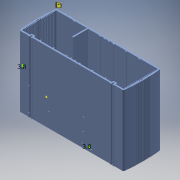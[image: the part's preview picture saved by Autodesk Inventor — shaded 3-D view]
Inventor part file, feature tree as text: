
AUTODESK INVENTOR PART (.ipt)
format: ipt  version: 2018 (Build 220112000, 112)  size: 1,293,312 bytes
history: native  units: mm
features: sketch x13, reference x7, extrude x6, other x4, projected_geometry x2, imported_body x1
ambient origin geometry x8: Origin, YZ Plane, XZ Plane, XY Plane, X Axis, Y Axis, Z Axis, Center Point
bodies: Body1 (feature_tree)
feature tree (33):
  other  "041800222_Profil_X_Dream_t220.1"
  imported_body  "Basis1"
  extrude  "Extrusion1"  Depth=4.2mm
  extrude  "Extrusion2"  Depth=93.5mm
  extrude  "Extrusion3"  Depth=8.0mm
  sketch  "Sketch5"  dims[d8=8.0mm d9=4.0mm d10=0.0mm]
  sketch  "Sketch6"  dims[d11=15.08mm d13=3.0mm]
  sketch  "Sketch7"  dims[d14=8.0mm d15=93.297949mm]
  sketch  "Sketch8"  dims[d16=3.0mm]
  sketch  "Sketch9"  dims[d17=8.0mm]
  extrude  "Extrusion6"  Depth=4.0mm TaperAngle=0.0deg
  sketch  "Sketch11"  dims[d20=3.8mm]
  sketch  "Sketch12"  dims[d23=3.8mm]
  extrude  "Extrusion7"  Depth=3.0mm
  extrude  "Extrusion9"  Depth=93.297949mm
  sketch  "Sketch2"  dims[d0=32.0mm d1=0.0mm d2=4.2mm]
  sketch  "Sketch3"  dims[d3=15.08mm d4=93.5mm]
  sketch  "Sketch4"  dims[d5=4.2mm d6=93.5mm d7=8.0mm]
  sketch  "Sketch10"  dims[d18=6.0mm d19=0.0mm]
  projected_geometry  "Projected Loop1"
  reference  "Reference1"
  sketch  "Sketch13"  dims[d26=10.0mm d27=0.0mm]
  reference  "Reference2"
  sketch  "Sketch14"  dims[d28=4.0mm d29=0.0mm d32=15.0mm d33=0.0mm]
  projected_geometry  "Projected Loop2"
  reference  "Reference3"
  reference  "Reference4"
  reference  "Reference5"
  reference  "Reference6"
  reference  "Reference8"
  other  "<userpath>\Documents\optoelectronics\CAD\Bigdriver_box\Big_housing.iam"
  other  "Big_housing.iam"
  other  "source:1"
